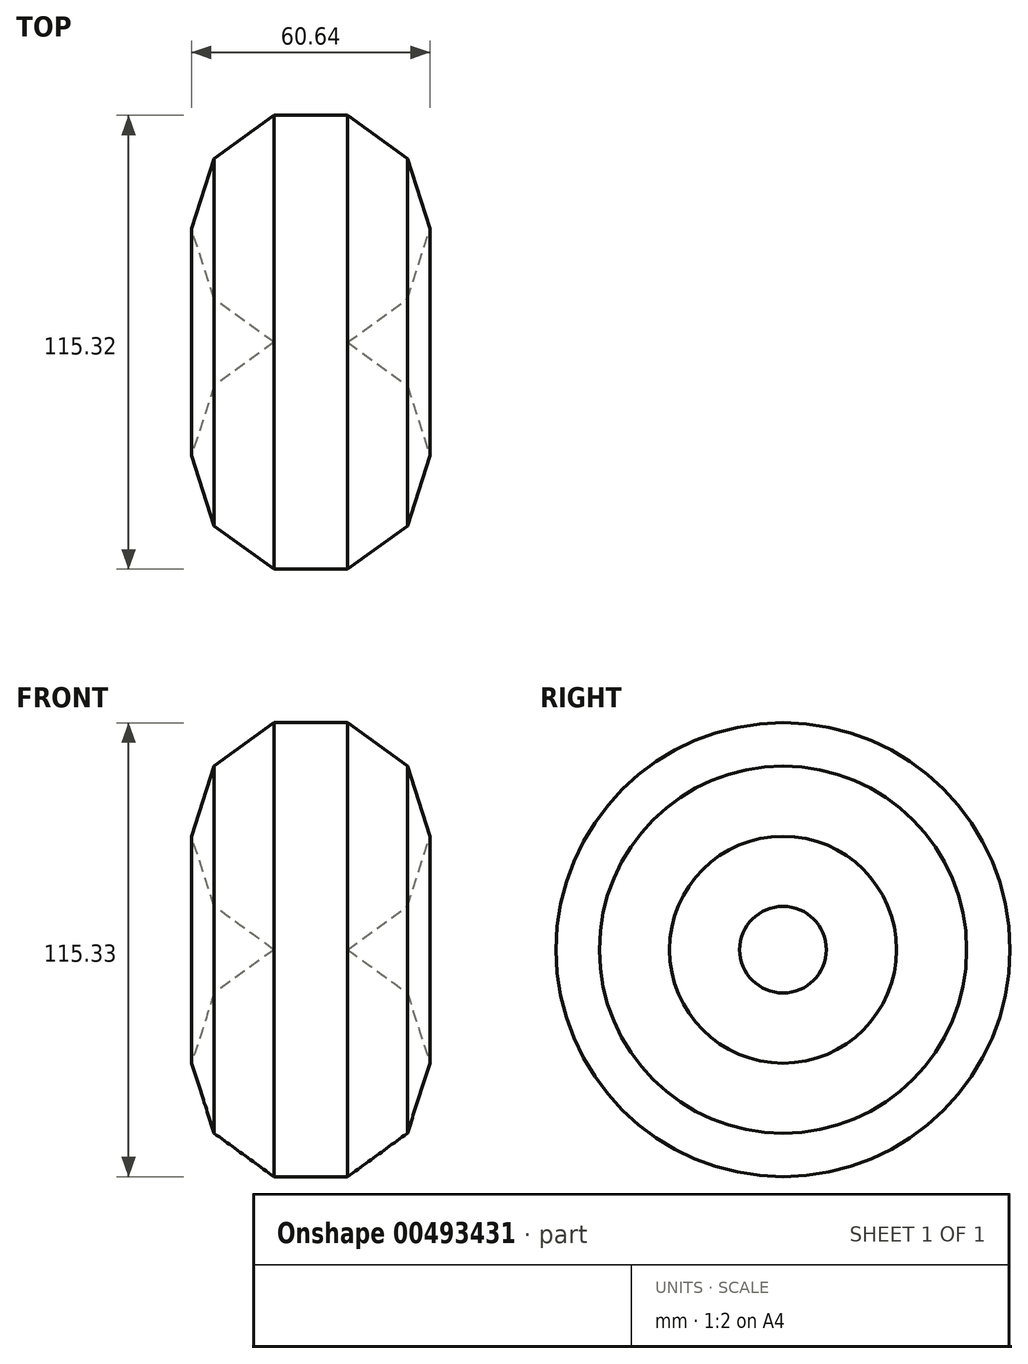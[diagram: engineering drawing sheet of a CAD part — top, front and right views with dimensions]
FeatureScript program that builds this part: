
annotation { "Feature Type Name" : "Feature", "Feature Type Description" : "" }
export const myFeature = defineFeature(function(context is Context, id is Id, definition is map)
    precondition{}
    {
        {
            var Q0;
            Q0=qCreatedBy(makeId("Front.planeOp"),FACE);
            var sketch = newSketch(context, id + "F0", { "sketchPlane" : qUnion([Q0])});
            skCircle(sketch, "E0.cCircle", {"center": v(0, 0) * mm, "radius": 28.83 * mm, "construction": true});
            skLineSegment(sketch, "E0.0", {"start": v(-9.37, 28.83) * mm, "end": v(9.37, 28.83) * mm});
            skLineSegment(sketch, "E0.1", {"start": v(9.37, 28.83) * mm, "end": v(24.53, 17.82) * mm});
            skLineSegment(sketch, "E0.2", {"start": v(24.53, 17.82) * mm, "end": v(30.32, 0) * mm});
            skLineSegment(sketch, "E0.3", {"start": v(30.32, 0) * mm, "end": v(24.53, -17.82) * mm});
            skLineSegment(sketch, "E0.4", {"start": v(24.53, -17.82) * mm, "end": v(9.37, -28.83) * mm});
            skLineSegment(sketch, "E0.5", {"start": v(9.37, -28.83) * mm, "end": v(-9.37, -28.83) * mm});
            skLineSegment(sketch, "E0.6", {"start": v(-9.37, -28.83) * mm, "end": v(-24.53, -17.82) * mm});
            skLineSegment(sketch, "E0.7", {"start": v(-24.53, -17.82) * mm, "end": v(-30.32, 0) * mm});
            skLineSegment(sketch, "E0.8", {"start": v(-30.32, 0) * mm, "end": v(-24.53, 17.82) * mm});
            skLineSegment(sketch, "E0.9", {"start": v(-24.53, 17.82) * mm, "end": v(-9.37, 28.83) * mm});
            skPoint(sketch, "E0.0.midPoint", {"position": v(0, 28.83) * mm});
            skSolve(sketch);
        }
        {
            var Q0;
            Q0=makeQuery(id+"F0.imprint","IMPRINT",FACE,{"disambiguationData":[TD([[makeQuery(id+"F0.imprint","IMPRINT",EDGE,{"derivedFrom":sQuery(id+"F0.wireOp",EDGE,"E0.0")}),-1.0]])]});
            var Q1;
            Q1=sQuery(id+"F0.wireOp",EDGE,"E0.5");
            revolve(context, id + "F1", {"entities" : qUnion([Q0]), "axis" : qUnion([Q1]), "revolveType" : RevolveType.FULL});
        }
    });
